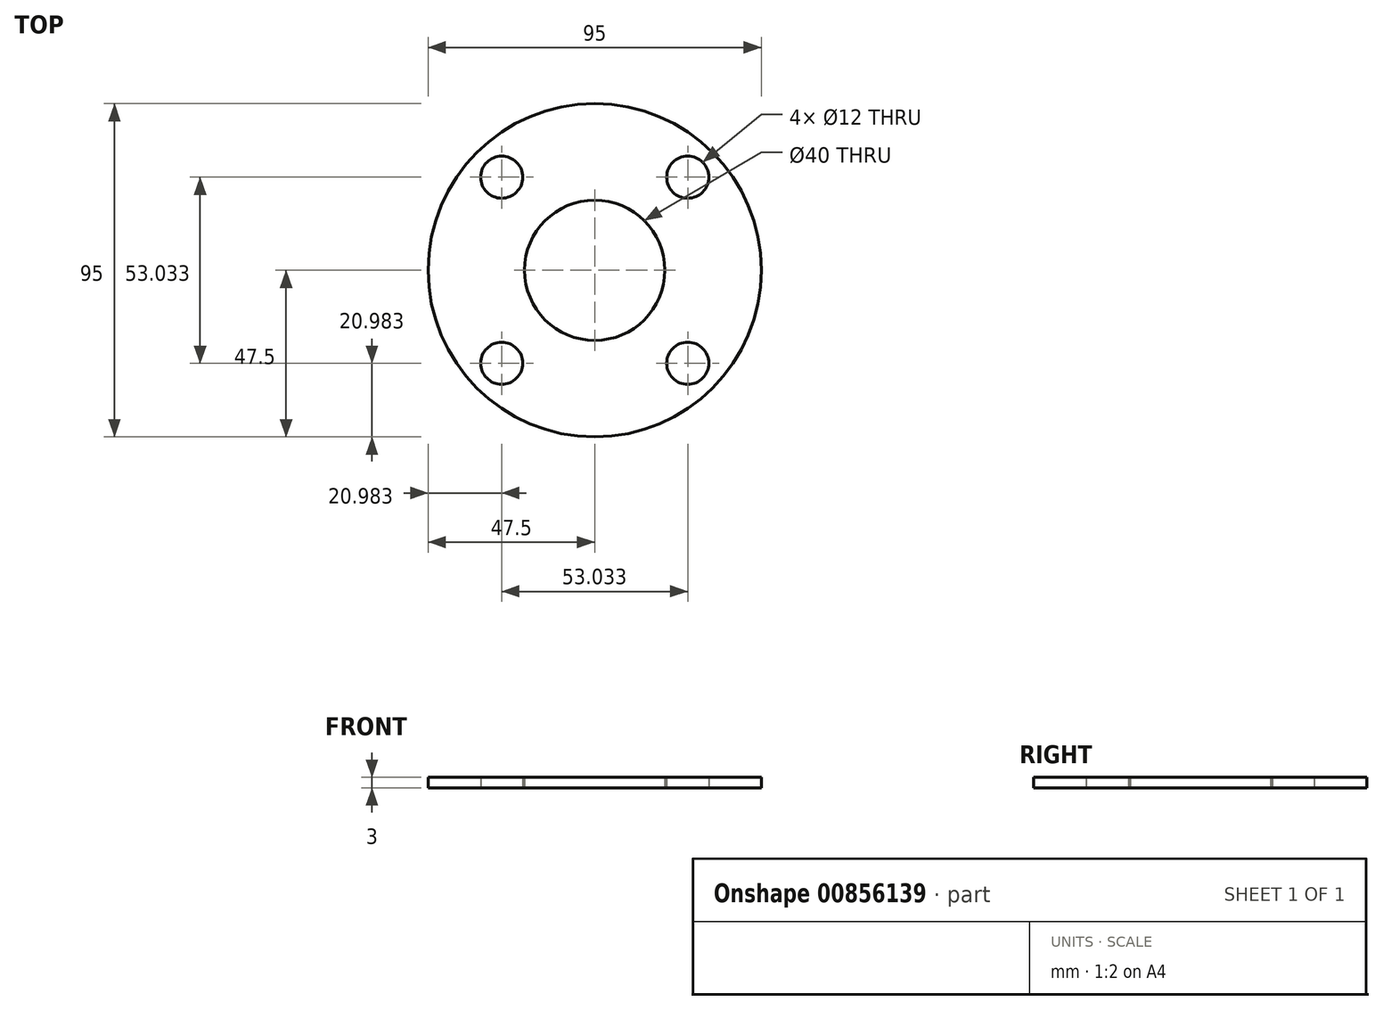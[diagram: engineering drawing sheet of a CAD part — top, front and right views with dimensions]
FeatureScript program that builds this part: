
annotation { "Feature Type Name" : "Feature", "Feature Type Description" : "" }
export const myFeature = defineFeature(function(context is Context, id is Id, definition is map)
    precondition{}
    {
        {
            var Q0;
            Q0=qCreatedBy(makeId("Top.planeOp"),FACE);
            var sketch = newSketch(context, id + "F0", { "sketchPlane" : qUnion([Q0])});
            skLineSegment(sketch, "E0", {"start": v(194.12, 0) * mm, "end": v(-195.43, 0) * mm, "construction": true});
            skLineSegment(sketch, "E1", {"start": v(0, 196.09) * mm, "end": v(0, -215.8) * mm, "construction": true});
            skCircle(sketch, "E2", {"center": v(0, 0) * mm, "radius": 37.5 * mm, "construction": true});
            skCircle(sketch, "E3", {"center": v(0, 0) * mm, "radius": 20 * mm});
            skCircle(sketch, "E4", {"center": v(0, 0) * mm, "radius": 47.5 * mm});
            skLineSegment(sketch, "E5", {"start": v(0, 0) * mm, "end": v(40.34, 40.34) * mm, "construction": true});
            skCircle(sketch, "E6", {"center": v(26.52, 26.52) * mm, "radius": 6 * mm});
            skCircle(sketch, "E7.1.0", {"center": v(-26.52, 26.52) * mm, "radius": 6 * mm});
            skCircle(sketch, "E7.2.0", {"center": v(-26.52, -26.52) * mm, "radius": 6 * mm});
            skCircle(sketch, "E7.3.0", {"center": v(26.52, -26.52) * mm, "radius": 6 * mm});
            skSolve(sketch);
        }
        {
            var Q0;
            Q0=makeQuery(id+"F0.imprint","IMPRINT",FACE,{"disambiguationData":[TD([[makeQuery(id+"F0.imprint","IMPRINT",EDGE,{"derivedFrom":sQuery(id+"F0.wireOp",EDGE,"E3")}),-1.0]])]});
            extrude(context, id + "F1", {"entities" : qUnion([Q0]), "depth" : 3 * mm, "offsetDistance" : 25 * mm});
        }
    });
